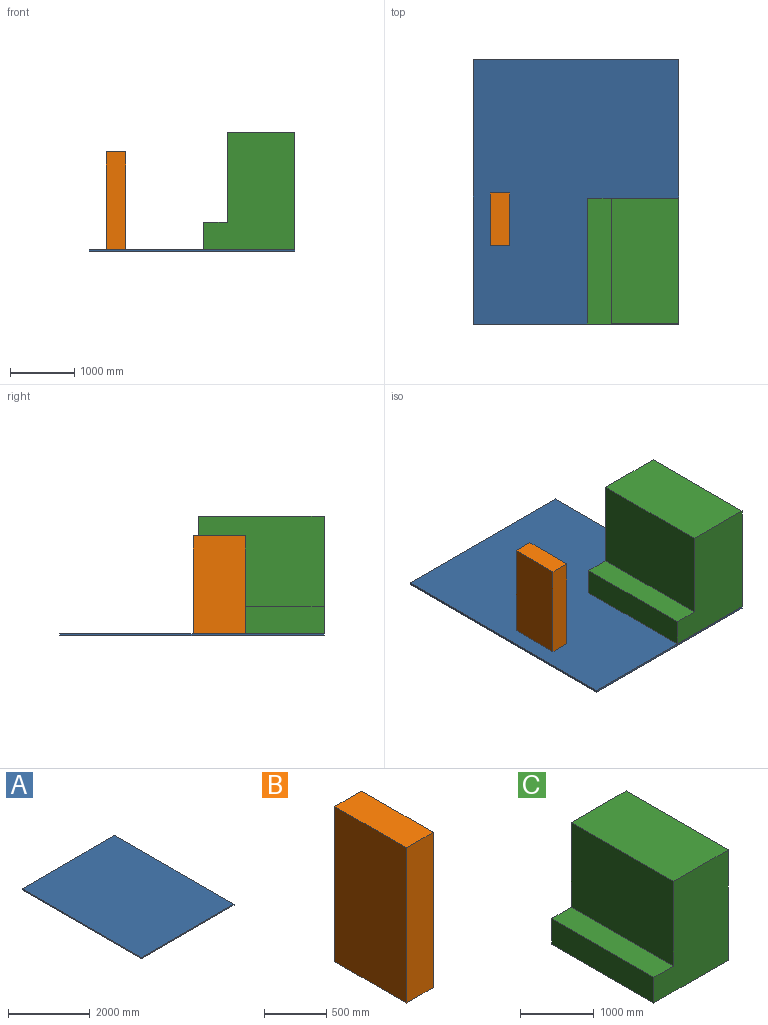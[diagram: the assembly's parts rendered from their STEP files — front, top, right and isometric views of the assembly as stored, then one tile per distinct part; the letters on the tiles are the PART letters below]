
ASSEMBLY  parts=3 mates=2
PART A: 6 faces, bbox 3200.4x4114.8x30.5 mm
  f0: plane 4114.8x30.48mm, normal (-1,0,0), area 125419.1mm2, adj f1,f3,f4,f5
  f1: plane 3200.4x30.48mm, normal (0,-1,0), area 97548.2mm2, adj f0,f2,f4,f5
  f2: plane 4114.8x30.48mm, normal (1,0,0), area 125419.1mm2, adj f1,f3,f4,f5
  f3: plane 3200.4x30.48mm, normal (0,1,0), area 97548.2mm2, adj f0,f2,f4,f5
  f4: plane 4114.8x3200.4mm, normal (0,0,1), area 13169005.9mm2, adj f0,f1,f2,f3
  f5: plane 4114.8x3200.4mm, normal (0,0,-1), area 13169005.9mm2, adj f0,f1,f2,f3
PART B: 6 faces, bbox 304.8x812.8x1524 mm
  f0: plane 1524x812.8mm, normal (-1,0,0), area 1238707.2mm2, adj f1,f3,f4,f5
  f1: plane 1524x304.8mm, normal (0,-1,0), area 464515.2mm2, adj f0,f2,f4,f5
  f2: plane 1524x812.8mm, normal (1,0,0), area 1238707.2mm2, adj f1,f3,f4,f5
  f3: plane 1524x304.8mm, normal (0,1,0), area 464515.2mm2, adj f0,f2,f4,f5
  f4: plane 812.8x304.8mm, normal (0,0,1), area 247741.4mm2, adj f0,f1,f2,f3
  f5: plane 812.8x304.8mm, normal (0,0,-1), area 247741.4mm2, adj f0,f1,f2,f3
PART C: 8 faces, bbox 1422.4x1955.8x1828.8 mm
  f0: plane 1828.8x1422.4mm, normal (0,-1,0), area 2077519.5mm2, adj f1,f2,f4,f5,f6,f7
  f1: plane 1955.8x1049.1mm, normal (0,0,1), area 2051831.3mm2, adj f0,f2,f3,f7
  f2: plane 1955.8x1828.8mm, normal (1,0,0), area 3576767mm2, adj f0,f1,f3,f5
  f3: plane 1828.8x1422.4mm, normal (0,1,0), area 2077519.5mm2, adj f1,f2,f4,f5,f6,f7
  f4: plane 1955.8x425.73mm, normal (-1,0,0), area 832639.1mm2, adj f0,f3,f5,f6
  f5: plane 1955.8x1422.4mm, normal (0,0,-1), area 2781929.9mm2, adj f0,f2,f3,f4
  f6: plane 1955.8x373.3mm, normal (0,0,1), area 730098.6mm2, adj f0,f3,f4,f7
  f7: plane 1955.8x1403.07mm, normal (-1,0,0), area 2744127.9mm2, adj f0,f1,f3,f6
PLACE A at identity
PLACE B t=(261.69,146.45,0)mm
PLACE C at identity
MATE fastened C.f2 <-> A.f2  axis (1,0,0) through (3200.4,0,30.48)mm
MATE planar A.f4 <-> B.f5  axis (0,0,1) through (1600.2,2057.4,30.48)mm
